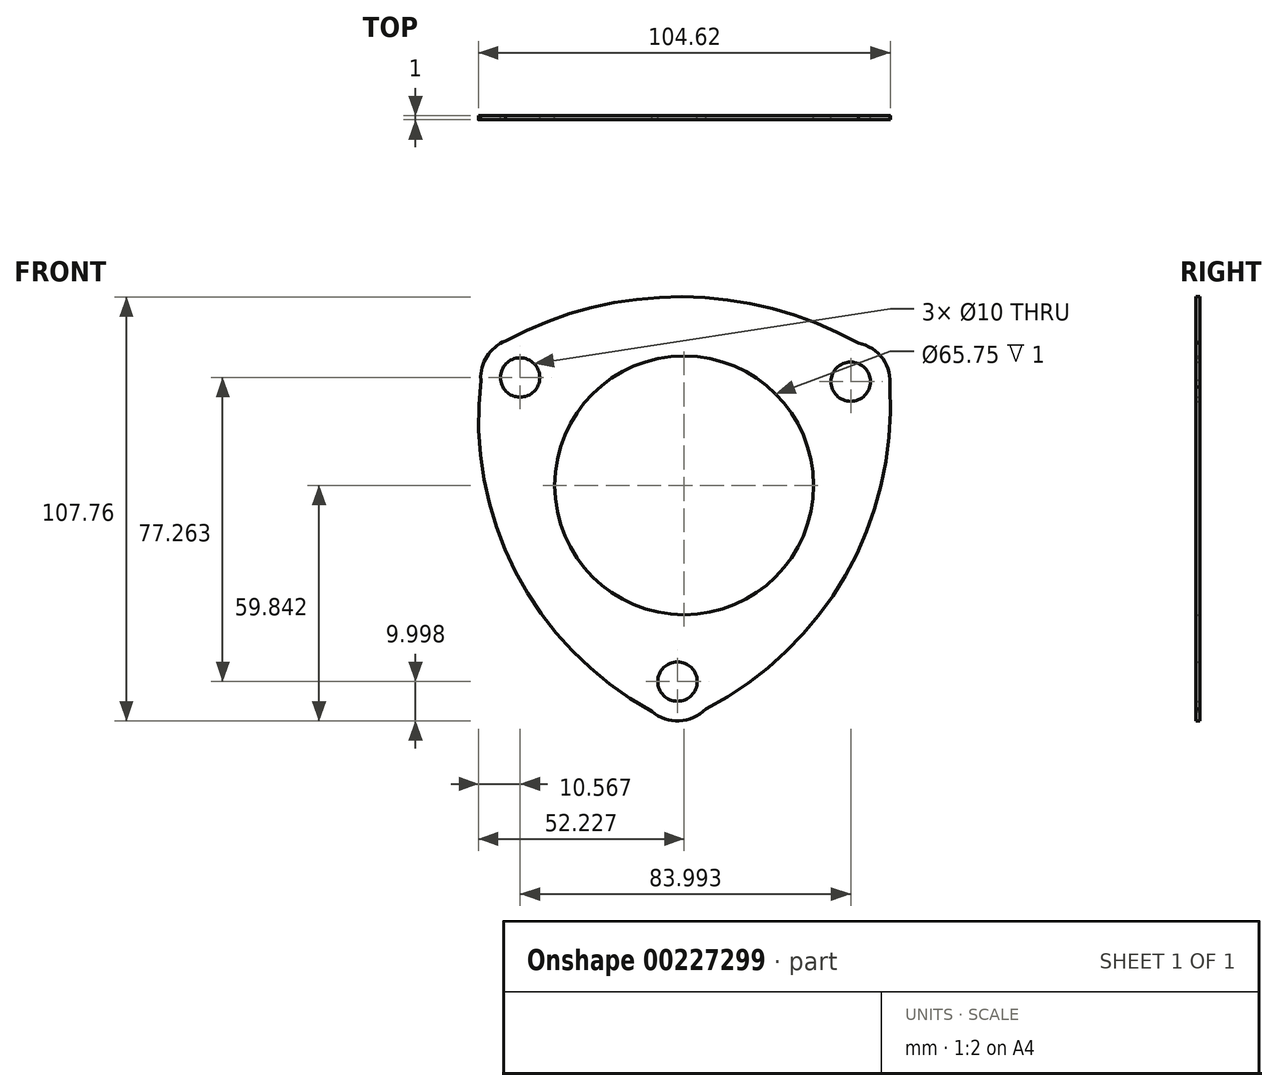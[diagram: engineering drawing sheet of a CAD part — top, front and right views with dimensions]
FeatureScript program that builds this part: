
annotation { "Feature Type Name" : "Feature", "Feature Type Description" : "" }
export const myFeature = defineFeature(function(context is Context, id is Id, definition is map)
    precondition{}
    {
        {
            var Q0;
            Q0=qCreatedBy(makeId("Front.planeOp"),FACE);
            var sketch = newSketch(context, id + "F0", { "sketchPlane" : qUnion([Q0])});
            skCircle(sketch, "E0", {"center": v(1.78, 9.77) * mm, "radius": 32.87 * mm});
            skCircle(sketch, "E1", {"center": v(44.11, 36.14) * mm, "radius": 5 * mm});
            skCircle(sketch, "E2", {"center": v(0.11, -40.07) * mm, "radius": 5 * mm});
            skCircle(sketch, "E3", {"center": v(-39.88, 37.2) * mm, "radius": 5 * mm});
            skArc(sketch, "E4", {"start": v(-43.6, 46.48) * mm, "mid": v(-48.33, 42.54) * mm, "end": v(-49.86, 36.58) * mm});
            skArc(sketch, "E5", {"start": v(54.02, 34.78) * mm, "mid": v(52.25, 41.94) * mm, "end": v(46.05, 45.95) * mm});
            skArc(sketch, "E6", {"start": v(-6.43, -47.63) * mm, "mid": v(0.54, -50.06) * mm, "end": v(7.28, -47.04) * mm});
            skArc(sketch, "E7", {"start": v(7.28, -47.04) * mm, "mid": v(42.8, -13.08) * mm, "end": v(54.02, 34.78) * mm});
            skArc(sketch, "E8", {"start": v(46.05, 45.95) * mm, "mid": v(1.3, 57.7) * mm, "end": v(-43.6, 46.48) * mm});
            skArc(sketch, "E9", {"start": v(-49.86, 36.58) * mm, "mid": v(-41.03, -12.17) * mm, "end": v(-6.43, -47.63) * mm});
            skSolve(sketch);
        }
        {
            var Q0;
            Q0=makeQuery(id+"F0.imprint","IMPRINT",FACE,{"disambiguationData":[TD([[makeQuery(id+"F0.imprint","IMPRINT",EDGE,{"derivedFrom":sQuery(id+"F0.wireOp",EDGE,"E0")}),-1.0]])]});
            extrude(context, id + "F1", {"entities" : qUnion([Q0]), "depth" : 1 * mm});
        }
    });
